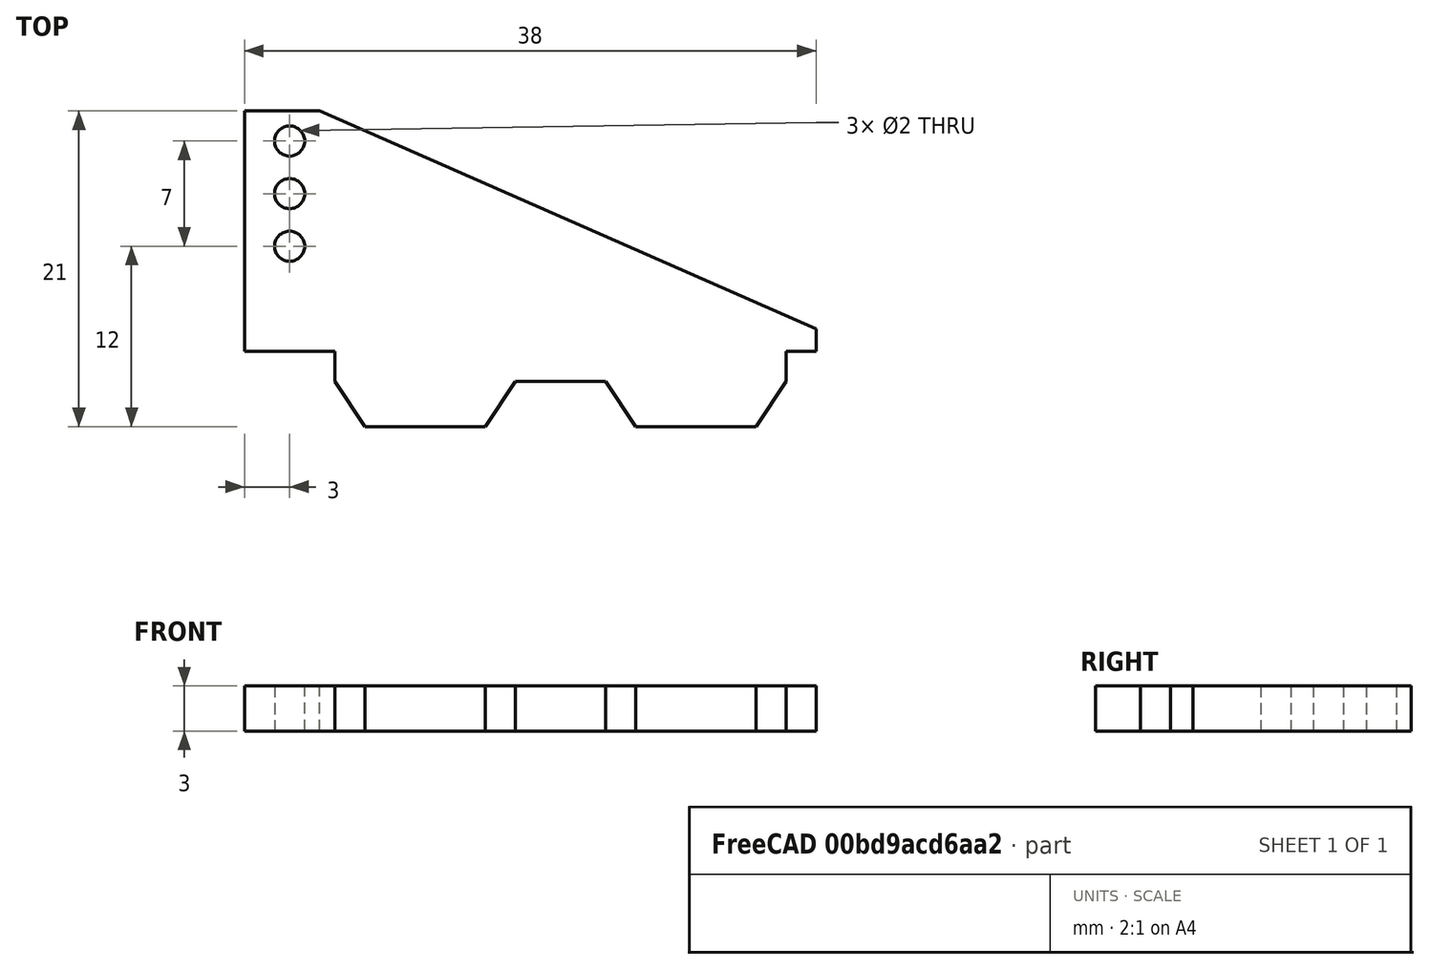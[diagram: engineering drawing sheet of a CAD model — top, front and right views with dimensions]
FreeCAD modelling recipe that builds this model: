
FCSTD DOCUMENT  (FreeCAD 0.19R)
Label: horn
License: All rights reserved
LicenseURL: http://en.wikipedia.org/wiki/All_rights_reserved
objects: Sketcher::SketchObject×1, PartDesign::Pad×1, PartDesign::Body×1
note: 4 computed .brp shape members not serialized (recipe doc carries the construction recipe); baked Part::Feature solids carry a one-line shape summary decoded from their .brp

FEATURE [Sketcher::SketchObject] Sketch
  FullyConstrained = true
  MapMode = 5
  Support = -> [XY_Plane]
  sketch-geometry (19):
    g0: LineSegment StartX=0 StartY=0 StartZ=0 EndX=8 EndY=0 EndZ=0
    g1: LineSegment StartX=8 StartY=0 StartZ=0 EndX=10 EndY=3 EndZ=0
    g2: LineSegment StartX=10 StartY=3 StartZ=0 EndX=16 EndY=3 EndZ=0
    g3: LineSegment StartX=16 StartY=3 StartZ=0 EndX=18 EndY=0 EndZ=0
    g4: LineSegment StartX=18 StartY=0 StartZ=0 EndX=26 EndY=0 EndZ=0
    g5: LineSegment StartX=26 StartY=0 StartZ=0 EndX=28 EndY=3 EndZ=0
    g6: LineSegment StartX=28 StartY=3 StartZ=0 EndX=28 EndY=5 EndZ=0
    g7: LineSegment StartX=0 StartY=0 StartZ=0 EndX=-2 EndY=3 EndZ=0
    g8: LineSegment StartX=-2 StartY=3 StartZ=0 EndX=-2 EndY=5 EndZ=0
    g9: LineSegment StartX=28 StartY=5 StartZ=0 EndX=30 EndY=5 EndZ=0
    g10: LineSegment StartX=-2 StartY=5 StartZ=0 EndX=-8 EndY=5 EndZ=0
    g11: LineSegment StartX=-8 StartY=5 StartZ=0 EndX=-8 EndY=21 EndZ=0
    g12: LineSegment StartX=-8 StartY=21 StartZ=0 EndX=-3 EndY=21 EndZ=0
    g13: LineSegment StartX=30 StartY=5 StartZ=0 EndX=30 EndY=6.5 EndZ=0
    g14: LineSegment StartX=30 StartY=6.5 StartZ=0 EndX=-3 EndY=21 EndZ=0
    g15: Circle CenterX=-5 CenterY=19 CenterZ=0 NormalX=0 NormalY=0 NormalZ=1 AngleXU=0 Radius=1
    g16: Circle CenterX=-5 CenterY=15.5 CenterZ=0 NormalX=0 NormalY=0 NormalZ=1 AngleXU=0 Radius=1
    g17: Circle CenterX=-5 CenterY=12 CenterZ=0 NormalX=0 NormalY=0 NormalZ=1 AngleXU=0 Radius=1
    g18: LineSegment StartX=-5 StartY=19 StartZ=0 EndX=-5 EndY=12 EndZ=0
  constraints (55):
    c: Coincident(g0,g-1)
    c: PointOnObject(g0,g-1)
    c: DistanceX(g0,g0) = 8
    c: Coincident(g1,g0)
    c: Coincident(g2,g1)
    c: Horizontal(g2)
    c: Coincident(g3,g2)
    c: PointOnObject(g3,g-1)
    c: DistanceX(g0,g1) = 2
    c: DistanceY(g0,g1) = 3
    c: DistanceX(g2,g2) = 6
    c: DistanceX(g2,g3) = 2
    c: Coincident(g4,g3)
    c: PointOnObject(g4,g-1)
    c: DistanceX(g4,g4) = 8
    c: Coincident(g5,g4)
    c: DistanceX(g4,g5) = 2
    c: DistanceY(g4,g5) = 3
    c: Coincident(g6,g5)
    c: Vertical(g6)
    c: DistanceY(g6,g6) = 2
    c: Coincident(g7,g0)
    c: DistanceX(g7,g0) = 2
    c: DistanceY(g0,g7) = 3
    c: Coincident(g8,g7)
    c: Vertical(g8)
    c: DistanceY(g8,g8) = 2
    c: Coincident(g9,g6)
    c: Horizontal(g9)
    c: DistanceX(g9,g9) = 2
    c: Coincident(g10,g8)
    c: Horizontal(g10)
    c: DistanceX(g10,g9) = 38
    c: Coincident(g11,g10)
    c: Vertical(g11)
    c: Coincident(g12,g11)
    c: Horizontal(g12)
    c: Coincident(g13,g9)
    c: Vertical(g13)
    c: Coincident(g14,g13)
    c: Coincident(g14,g12)
    c: DistanceY(g13,g13) = 1.5
    c: DistanceY(g11,g11) = 16
    c: DistanceX(g12,g12) = 5
    c: Equal(g17,g16)
    c: Equal(g16,g15)
    c: Diameter(g15) = 2
    c: DistanceX(g11,g15) = 3
    c: Coincident(g18,g15)
    c: Vertical(g18)
    c: DistanceY(g18,g18) = 7
    c: DistanceY(g15,g11) = 2
    c: PointOnObject(g16,g18)
    c: Coincident(g17,g18)
    c: DistanceY(g16,g15) = 3.5
FEATURE [PartDesign::Pad] Pad
  Direction = (1,1,1)
  Length = 3
  Length2 = 100
  Profile = -> Sketch
  Type = 0
FEATURE [PartDesign::Body] Body
  Group = -> [Sketch,Pad]
  Origin = -> Origin
  Tip = -> Pad
